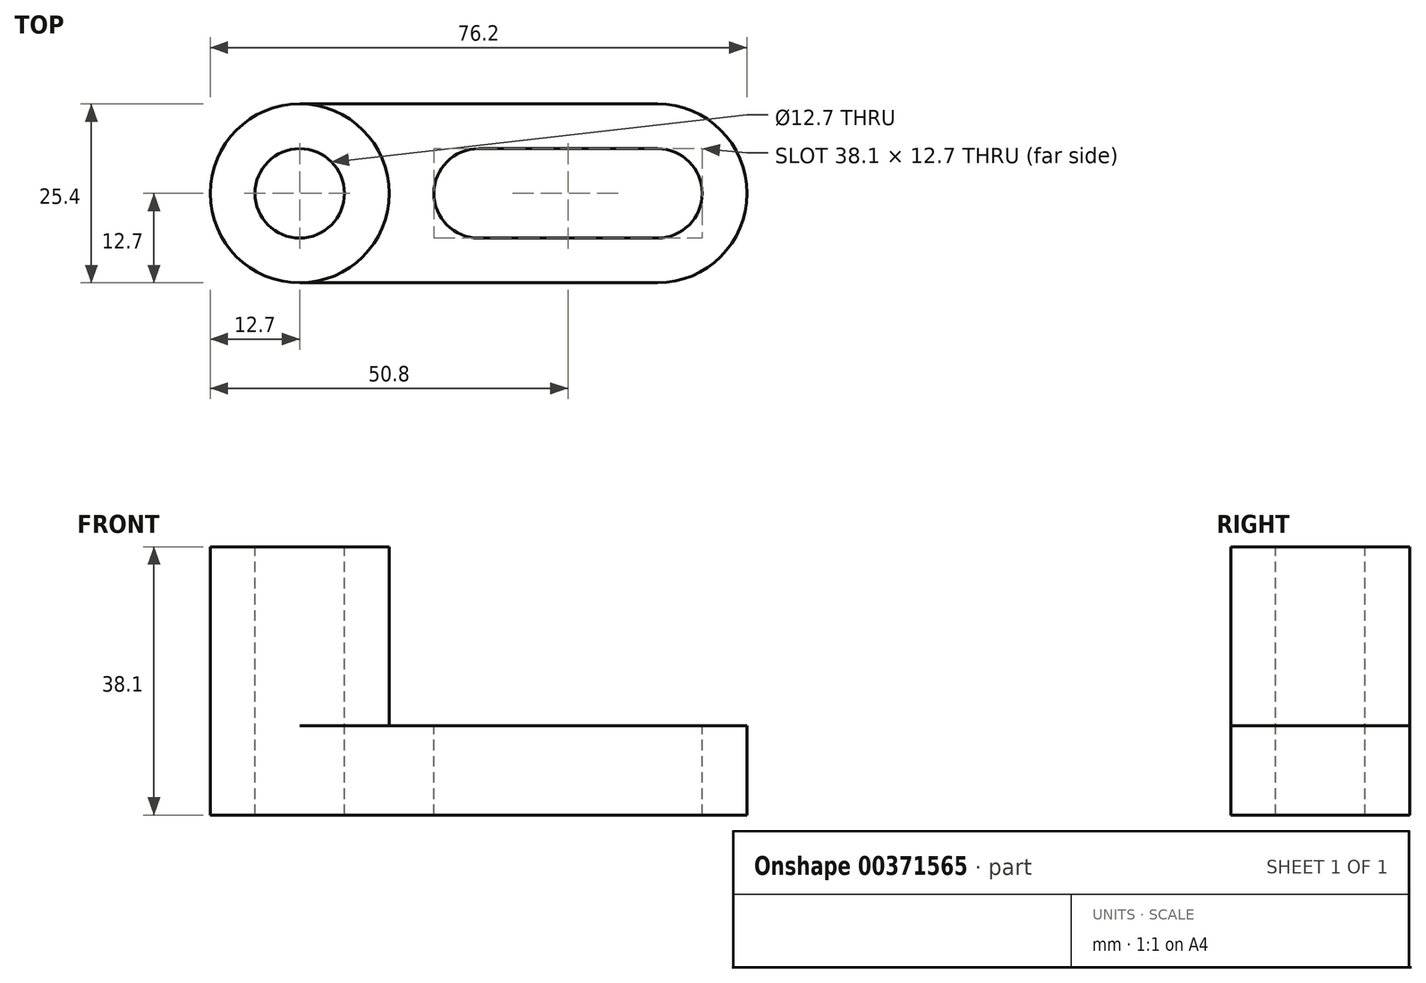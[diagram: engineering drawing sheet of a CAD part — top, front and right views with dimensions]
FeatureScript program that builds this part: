
annotation { "Feature Type Name" : "Feature", "Feature Type Description" : "" }
export const myFeature = defineFeature(function(context is Context, id is Id, definition is map)
    precondition{}
    {
        {
            var Q0;
            Q0=qCreatedBy(makeId("Front.planeOp"),FACE);
            var sketch = newSketch(context, id + "F0", { "sketchPlane" : qUnion([Q0])});
            skLineSegment(sketch, "E0", {"start": v(0, 0) * mm, "end": v(76.2, 0) * mm});
            skLineSegment(sketch, "E1", {"start": v(76.2, 0) * mm, "end": v(76.2, 12.7) * mm});
            skLineSegment(sketch, "E2", {"start": v(76.2, 12.7) * mm, "end": v(25.4, 12.7) * mm});
            skLineSegment(sketch, "E3", {"start": v(25.4, 12.7) * mm, "end": v(25.4, 38.1) * mm});
            skLineSegment(sketch, "E4", {"start": v(25.4, 38.1) * mm, "end": v(0, 38.1) * mm});
            skLineSegment(sketch, "E5", {"start": v(0, 38.1) * mm, "end": v(0, 0) * mm});
            skSolve(sketch);
        }
        {
            var Q0;
            Q0=makeQuery(id+"F0.imprint","IMPRINT",FACE,{"disambiguationData":[TD([[makeQuery(id+"F0.imprint","IMPRINT",EDGE,{"derivedFrom":sQuery(id+"F0.wireOp",EDGE,"E0")}),1.0]])]});
            extrude(context, id + "F1", {"entities" : qUnion([Q0]), "depth" : 25.4 * mm});
        }
        {
            var Q0;
            Q0=makeQuery(id+"F1.opExtrude","SWEPT_FACE",FACE,{"disambiguationData":[OSD([sQuery(id+"F0.wireOp",EDGE,"E4")])]});
            var sketch = newSketch(context, id + "F2", { "sketchPlane" : qUnion([Q0])});
            skCircle(sketch, "E6", {"center": v(12.7, -12.7) * mm, "radius": 6.35 * mm});
            skPoint(sketch, "E6.centerSnap0", {"position": v(12.7, 0) * mm});
            skCircle(sketch, "E7", {"center": v(12.7, -12.7) * mm, "radius": 12.7 * mm});
            skSolve(sketch);
        }
        {
            var Q0;
            Q0=makeQuery(id+"F2.imprint","IMPRINT",FACE,{"disambiguationData":[TD([[makeQuery(id+"F2.imprint","IMPRINT",EDGE,{"derivedFrom":sQuery(id+"F2.wireOp",EDGE,"E6")}),1.0]])]});
            var Q1;
            {var subQ0=sQuery(id+"F2.wireOp",EDGE,"E7");var subQ1=sQuery(id+"F0.wireOp",EDGE,"E4");var subQ2=makeQuery(id+"F1.opExtrude","CAP_EDGE",EDGE,{"disambiguationData":[OSD([subQ1])],"isStart":true});var subQ3=makeQuery(id+"F2.imprint","INTERSECT",VERTEX,{"derivedFrom":[subQ2,subQ0]});Q1=makeQuery(id+"F2.imprint","IMPRINT",FACE,{"disambiguationData":[TD([[makeQuery(id+"F2.imprint","IMPRINT",EDGE,{"disambiguationData":[TD([[subQ3,-1.0]])],"derivedFrom":subQ0}),-1.0]])]});}
            var Q2;
            {var subQ0=sQuery(id+"F2.wireOp",EDGE,"E7");var subQ1=sQuery(id+"F0.wireOp",EDGE,"E4");var subQ4=makeQuery(id+"F1.opExtrude","CAP_EDGE",EDGE,{"disambiguationData":[OSD([subQ1])],"isStart":false});var subQ5=makeQuery(id+"F2.imprint","INTERSECT",VERTEX,{"derivedFrom":[subQ4,subQ0]});Q2=makeQuery(id+"F2.imprint","IMPRINT",FACE,{"disambiguationData":[TD([[makeQuery(id+"F2.imprint","IMPRINT",EDGE,{"disambiguationData":[TD([[subQ5,1.0]])],"derivedFrom":subQ0}),-1.0]])]});}
            extrude(context, id + "F3", {"entities" : qUnion([Q0, Q1, Q2]), "operationType" : NewBodyOperationType.REMOVE, "oppositeDirection" : true, "depth" : 38.1 * mm});
        }
        {
            var Q0;
            Q0=makeQuery(id+"F1.opExtrude","SWEPT_FACE",FACE,{"disambiguationData":[OSD([sQuery(id+"F0.wireOp",EDGE,"E4")])]});
            var sketch = newSketch(context, id + "F4", { "sketchPlane" : qUnion([Q0])});
            skCircle(sketch, "E8", {"center": v(12.7, -12.7) * mm, "radius": 12.7 * mm});
            skSolve(sketch);
        }
        {
            var Q0;
            {var subQ1=sQuery(id+"F0.wireOp",EDGE,"E4");var subQ2=makeQuery(id+"F1.opExtrude","CAP_EDGE",EDGE,{"disambiguationData":[OSD([subQ1])],"isStart":true});Q0=makeQuery(id+"F4.imprint","IMPRINT",FACE,{"disambiguationData":[TD([[makeQuery(id+"F4.imprint","IMPRINT",EDGE,{"derivedFrom":subQ2}),1.0]])]});}
            var Q1;
            {var subQ1=sQuery(id+"F0.wireOp",EDGE,"E4");var subQ2=makeQuery(id+"F1.opExtrude","CAP_EDGE",EDGE,{"disambiguationData":[OSD([subQ1])],"isStart":false});Q1=makeQuery(id+"F4.imprint","IMPRINT",FACE,{"disambiguationData":[TD([[makeQuery(id+"F4.imprint","IMPRINT",EDGE,{"derivedFrom":subQ2}),-1.0]])]});}
            extrude(context, id + "F5", {"entities" : qUnion([Q0, Q1]), "operationType" : NewBodyOperationType.REMOVE, "oppositeDirection" : true, "depth" : 25.4 * mm});
        }
        {
            var Q0;
            {var subQ0=sQuery(id+"F0.wireOp",EDGE,"E4");var subQ1=makeQuery(id+"F1.opExtrude","CAP_EDGE",EDGE,{"disambiguationData":[OSD([subQ0])],"isStart":false});var subQ2=sQuery(id+"F0.wireOp",EDGE,"E3");var subQ3=makeQuery(id+"F1.opExtrude","SWEPT_EDGE",EDGE,{"disambiguationData":[OSD([subQ2,subQ0])]});var subQ4=sQuery(id+"F4.wireOp",EDGE,"E8");var subQ6=makeQuery(id+"F1.opExtrude","CAP_EDGE",EDGE,{"disambiguationData":[OSD([subQ0])],"isStart":true});Q0=makeQuery(id+"F5.boolean.opBoolean","MERGE",FACE,{"derivedFrom":[makeQuery(id+"F1.opExtrude","SWEPT_FACE",FACE,{"disambiguationData":[OSD([sQuery(id+"F0.wireOp",EDGE,"E2")])]}),makeQuery(id+"F5.opExtrude","CAP_FACE",FACE,{"disambiguationData":[OSD([subQ2,subQ0,subQ4]),TDD([makeQuery(id+"F4.imprint","IMPRINT",EDGE,{"disambiguationData":[TD([[makeQuery(id+"F4.imprint","INTERSECT",VERTEX,{"derivedFrom":[subQ6,subQ4]}),1.0]])],"derivedFrom":subQ4}),makeQuery(id+"F4.imprint","IMPRINT",EDGE,{"derivedFrom":subQ6}),makeQuery(id+"F4.imprint","IMPRINT",EDGE,{"disambiguationData":[TD([[makeQuery(id+"F4.imprint","INTERSECT",VERTEX,{"derivedFrom":[subQ3,subQ6]}),1.0]])],"derivedFrom":subQ3})])],"isStart":false}),makeQuery(id+"F5.opExtrude","CAP_FACE",FACE,{"disambiguationData":[OSD([subQ2,subQ0,subQ4]),TDD([makeQuery(id+"F4.imprint","IMPRINT",EDGE,{"disambiguationData":[TD([[makeQuery(id+"F4.imprint","INTERSECT",VERTEX,{"derivedFrom":[subQ1,subQ4]}),-1.0]])],"derivedFrom":subQ4}),makeQuery(id+"F4.imprint","IMPRINT",EDGE,{"derivedFrom":subQ1}),makeQuery(id+"F4.imprint","IMPRINT",EDGE,{"disambiguationData":[TD([[makeQuery(id+"F4.imprint","INTERSECT",VERTEX,{"derivedFrom":[subQ3,subQ1]}),-1.0]])],"derivedFrom":subQ3})])],"isStart":false})]});}
            var sketch = newSketch(context, id + "F6", { "sketchPlane" : qUnion([Q0])});
            skCircle(sketch, "E9", {"center": v(63.5, -12.7) * mm, "radius": 6.35 * mm});
            skPoint(sketch, "E9.centerSnap0", {"position": v(76.2, -12.7) * mm});
            skCircle(sketch, "E10", {"center": v(38.1, -12.7) * mm, "radius": 6.35 * mm});
            skPoint(sketch, "E10.centerSnap0", {"position": v(25.4, -12.7) * mm});
            skLineSegment(sketch, "E11", {"start": v(38.1, -6.35) * mm, "end": v(63.5, -6.35) * mm});
            skLineSegment(sketch, "E12", {"start": v(38.1, -19.05) * mm, "end": v(63.5, -19.05) * mm});
            skArc(sketch, "E13", {"start": v(63.5, -25.4) * mm, "mid": v(76.2, -12.7) * mm, "end": v(63.5, 0) * mm});
            skSolve(sketch);
        }
        {
            var Q0;
            {var subQ0=sQuery(id+"F6.wireOp",EDGE,"E10");var subQ1=makeQuery(id+"F6.imprint","INTERSECT",VERTEX,{"derivedFrom":[subQ0,sQuery(id+"F6.wireOp",EDGE,"E11")]});Q0=makeQuery(id+"F6.imprint","IMPRINT",FACE,{"disambiguationData":[TD([[makeQuery(id+"F6.imprint","IMPRINT",EDGE,{"disambiguationData":[TD([[subQ1,-1.0]])],"derivedFrom":subQ0}),1.0]])]});}
            var Q1;
            {var subQ0=sQuery(id+"F6.wireOp",EDGE,"E11");Q1=makeQuery(id+"F6.imprint","IMPRINT",FACE,{"disambiguationData":[TD([[makeQuery(id+"F6.imprint","IMPRINT",EDGE,{"derivedFrom":subQ0}),-1.0]])]});}
            var Q2;
            {var subQ0=sQuery(id+"F6.wireOp",EDGE,"E9");var subQ1=makeQuery(id+"F6.imprint","INTERSECT",VERTEX,{"derivedFrom":[subQ0,sQuery(id+"F6.wireOp",EDGE,"E11")]});Q2=makeQuery(id+"F6.imprint","IMPRINT",FACE,{"disambiguationData":[TD([[makeQuery(id+"F6.imprint","IMPRINT",EDGE,{"disambiguationData":[TD([[subQ1,-1.0]])],"derivedFrom":subQ0}),1.0]])]});}
            var Q3;
            {var subQ0=sQuery(id+"F6.wireOp",EDGE,"E13");var subQ2=sQuery(id+"F0.wireOp",EDGE,"E2");var subQ5=makeQuery(id+"F1.opExtrude","SWEPT_EDGE",EDGE,{"disambiguationData":[OSD([sQuery(id+"F0.wireOp",EDGE,"E1"),subQ2])]});var subQ6=makeQuery(id+"F6.imprint","INTERSECT",VERTEX,{"derivedFrom":[subQ5,subQ0]});Q3=makeQuery(id+"F6.imprint","IMPRINT",FACE,{"disambiguationData":[TD([[makeQuery(id+"F6.imprint","IMPRINT",EDGE,{"disambiguationData":[TD([[subQ6,-1.0]])],"derivedFrom":subQ0}),-1.0]])]});}
            var Q4;
            {var subQ0=sQuery(id+"F6.wireOp",EDGE,"E13");var subQ2=sQuery(id+"F0.wireOp",EDGE,"E2");var subQ5=makeQuery(id+"F1.opExtrude","SWEPT_EDGE",EDGE,{"disambiguationData":[OSD([sQuery(id+"F0.wireOp",EDGE,"E1"),subQ2])]});var subQ6=makeQuery(id+"F6.imprint","INTERSECT",VERTEX,{"derivedFrom":[subQ5,subQ0]});Q4=makeQuery(id+"F6.imprint","IMPRINT",FACE,{"disambiguationData":[TD([[makeQuery(id+"F6.imprint","IMPRINT",EDGE,{"disambiguationData":[TD([[subQ6,1.0]])],"derivedFrom":subQ0}),-1.0]])]});}
            extrude(context, id + "F7", {"entities" : qUnion([Q0, Q1, Q2, Q3, Q4]), "operationType" : NewBodyOperationType.REMOVE, "oppositeDirection" : true, "depth" : 25.4 * mm});
        }
    });
